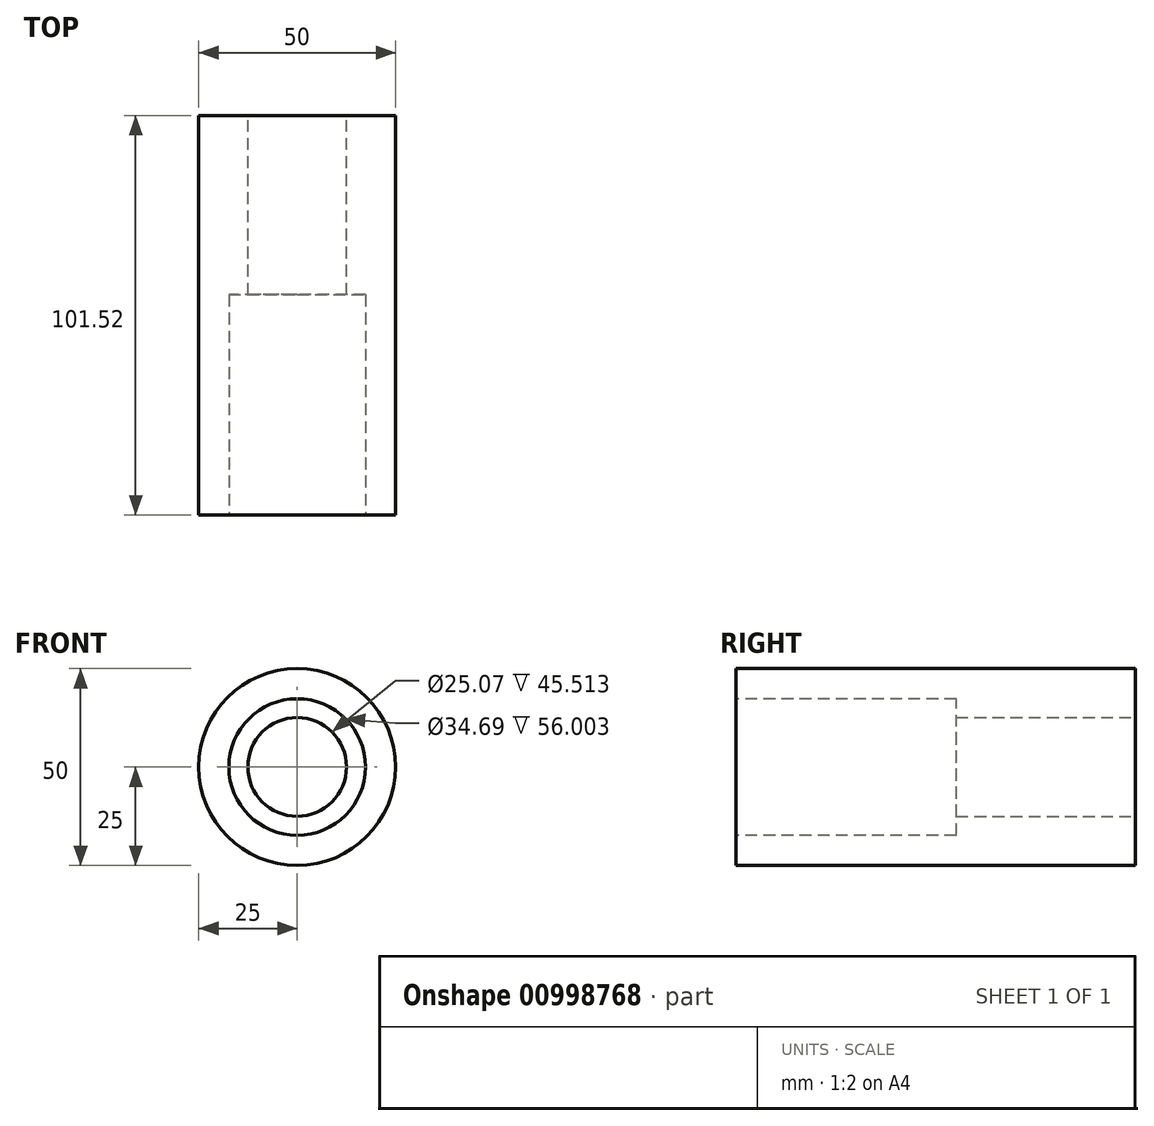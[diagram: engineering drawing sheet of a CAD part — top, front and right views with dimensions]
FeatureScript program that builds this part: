
annotation { "Feature Type Name" : "Feature", "Feature Type Description" : "" }
export const myFeature = defineFeature(function(context is Context, id is Id, definition is map)
    precondition{}
    {
        {
            var Q0;
            Q0=qCreatedBy(makeId("Front.planeOp"),FACE);
            var sketch = newSketch(context, id + "F0", { "sketchPlane" : qUnion([Q0])});
            skCircle(sketch, "E0", {"center": v(0, 0) * mm, "radius": 25 * mm});
            skSolve(sketch);
        }
        {
            var Q0;
            Q0 = qSketchRegion(id + "F0", true);
            var Q1;
            Q1=sQuery(id+"F0.wireOp",EDGE,"E0");
            extrude(context, id + "F1", {"entities" : qUnion([Q0]), "surfaceEntities" : qUnion([Q1]), "depth" : 101.52 * mm, "offsetDistance" : 25.4 * mm});
        }
        {
            var Q0;
            Q0=makeQuery(id+"F1.opExtrude","CAP_FACE",FACE,{"disambiguationData":[OSD([sQuery(id+"F0.wireOp",EDGE,"E0")])],"isStart":true});
            var sketch = newSketch(context, id + "F2", { "sketchPlane" : qUnion([Q0])});
            skCircle(sketch, "E1", {"center": v(0, 0) * mm, "radius": 12.54 * mm});
            skSolve(sketch);
        }
        {
            var Q0;
            Q0 = qSketchRegion(id + "F2", true);
            extrude(context, id + "F3", {"entities" : qUnion([Q0]), "operationType" : NewBodyOperationType.REMOVE, "oppositeDirection" : true, "depth" : 50.18 * mm, "offsetDistance" : 25.4 * mm});
        }
        {
            var Q0;
            Q0=makeQuery(id+"F1.opExtrude","CAP_FACE",FACE,{"disambiguationData":[OSD([sQuery(id+"F0.wireOp",EDGE,"E0")])],"isStart":false});
            var sketch = newSketch(context, id + "F4", { "sketchPlane" : qUnion([Q0])});
            skCircle(sketch, "E2", {"center": v(0, 0) * mm, "radius": 17.35 * mm});
            skSolve(sketch);
        }
        {
            var Q0;
            Q0=makeQuery(id+"F4.imprint","IMPRINT",FACE,{"disambiguationData":[TD([[makeQuery(id+"F4.imprint","IMPRINT",EDGE,{"derivedFrom":sQuery(id+"F4.wireOp",EDGE,"E2")}),1.0]])]});
            extrude(context, id + "F5", {"entities" : qUnion([Q0]), "operationType" : NewBodyOperationType.REMOVE, "oppositeDirection" : true, "depth" : 56 * mm, "offsetDistance" : 25.4 * mm});
        }
    });
